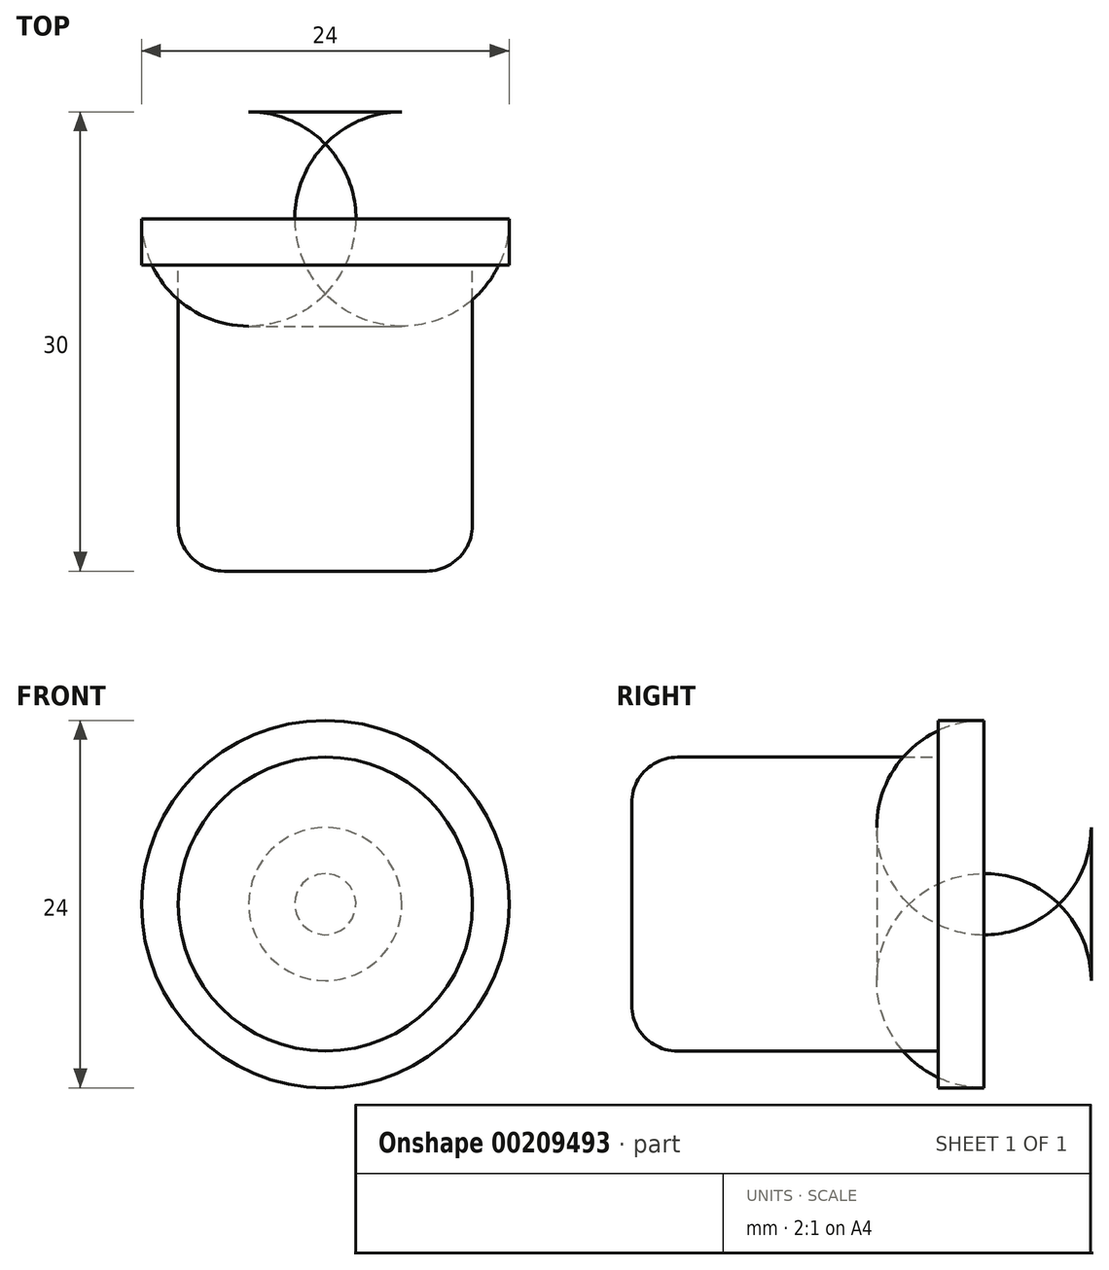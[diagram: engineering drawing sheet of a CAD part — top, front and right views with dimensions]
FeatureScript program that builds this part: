
annotation { "Feature Type Name" : "Feature", "Feature Type Description" : "" }
export const myFeature = defineFeature(function(context is Context, id is Id, definition is map)
    precondition{}
    {
        {
            var Q0;
            Q0=qCreatedBy(makeId("Front.planeOp"),FACE);
            var sketch = newSketch(context, id + "F0", { "sketchPlane" : qUnion([Q0])});
            skCircle(sketch, "E0", {"center": v(0, 0) * mm, "radius": 12 * mm});
            skSolve(sketch);
        }
        {
            var Q0;
            Q0=qCreatedBy(makeId("Front.planeOp"),FACE);
            var sketch = newSketch(context, id + "F1", { "sketchPlane" : qUnion([Q0])});
            skCircle(sketch, "E1", {"center": v(0, 0) * mm, "radius": 9.6 * mm});
            skSolve(sketch);
        }
        {
            var Q0;
            Q0 = qSketchRegion(id + "F1", true);
            extrude(context, id + "F2", {"entities" : qUnion([Q0]), "flatOperationType" : FlatOperationType.REMOVE, "offsetDistance" : 25 * mm, "depth" : 20 * mm, "domain" : OperationDomain.MODEL});
        }
        {
            var Q0;
            Q0 = qSketchRegion(id + "F0", true);
            extrude(context, id + "F3", {"entities" : qUnion([Q0]), "operationType" : NewBodyOperationType.ADD, "oppositeDirection" : true, "depth" : 10 * mm});
        }
        {
            var Q0;
            Q0=makeQuery(id+"F3.opExtrude","CAP_EDGE",EDGE,{"disambiguationData":[OSD([sQuery(id+"F0.wireOp",EDGE,"E0")])],"isStart":false});
            fillet(context, id + "F4", {"entities" : qUnion([Q0]), "radius" : 7 * mm, "tangentPropagation" : true, "allowEdgeOverflow" : false});
        }
        {
            var Q0;
            Q0=makeQuery(id+"F2.opExtrude","CAP_EDGE",EDGE,{"disambiguationData":[OSD([sQuery(id+"F1.wireOp",EDGE,"E1")])],"isStart":false});
            fillet(context, id + "F5", {"entities" : qUnion([Q0]), "radius" : 3 * mm, "tangentPropagation" : true, "allowEdgeOverflow" : false});
        }
    });
